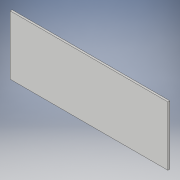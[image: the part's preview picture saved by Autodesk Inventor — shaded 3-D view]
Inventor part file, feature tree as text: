
AUTODESK INVENTOR PART (.ipt)
format: ipt  version: 2018 (Build 220112000, 112)  size: 88,576 bytes
history: native  units: in
note: dims shown in document units (in); Inventor stores cm internally (conversion verified against a paired STEP export)
features: extrude x1, sketch x1
ambient origin geometry x8: Origin, YZ Plane, XZ Plane, XY Plane, X Axis, Y Axis, Z Axis, Center Point
bodies: Solid1 (feature_tree)
feature tree (2):
  extrude  "Extrusion1"  Depth=118.1102in
  sketch  "Sketch1"  dims[d0=314.9606in d1=118.1102in d2=3.937in d3=0.0in]
